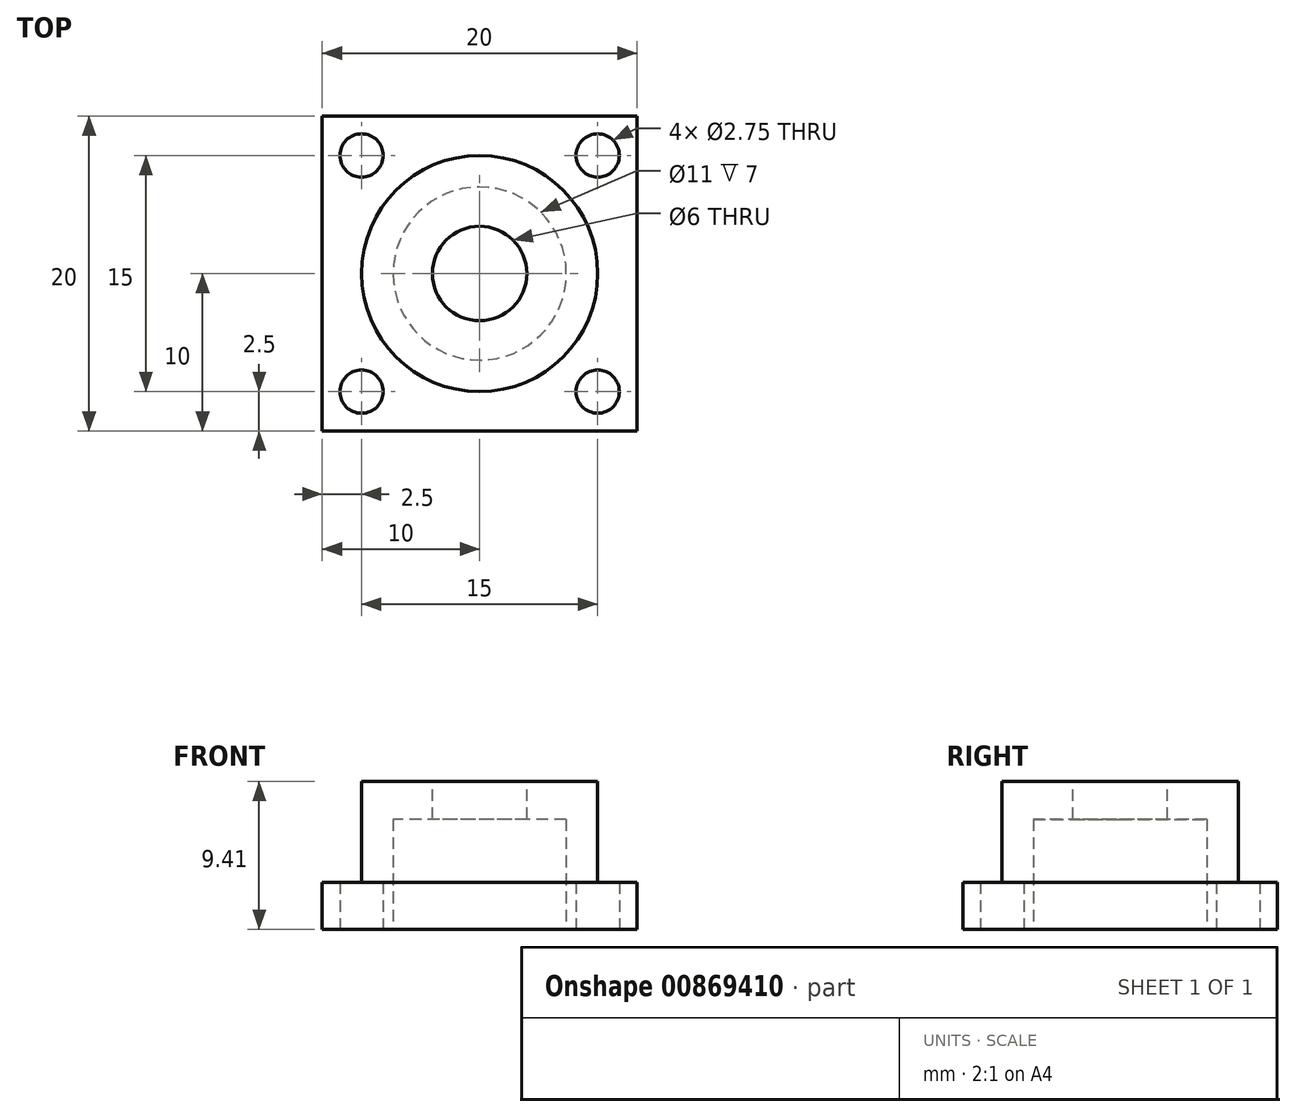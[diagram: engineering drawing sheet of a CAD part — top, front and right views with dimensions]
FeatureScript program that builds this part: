
annotation { "Feature Type Name" : "Feature", "Feature Type Description" : "" }
export const myFeature = defineFeature(function(context is Context, id is Id, definition is map)
    precondition{}
    {
        {
            var Q0;
            Q0=qCreatedBy(makeId("Top.planeOp"),FACE);
            var sketch = newSketch(context, id + "F0", { "sketchPlane" : qUnion([Q0])});
            skLineSegment(sketch, "E0.bottom", {"start": v(0, 0) * mm, "end": v(20, 0) * mm});
            skLineSegment(sketch, "E0.top", {"start": v(0, 20) * mm, "end": v(20, 20) * mm});
            skLineSegment(sketch, "E0.left", {"start": v(0, 0) * mm, "end": v(0, 20) * mm});
            skLineSegment(sketch, "E0.right", {"start": v(20, 0) * mm, "end": v(20, 20) * mm});
            skLineSegment(sketch, "E1", {"start": v(0, 10) * mm, "end": v(20, 10) * mm, "construction": true});
            skLineSegment(sketch, "E2", {"start": v(10, 0) * mm, "end": v(10, 20) * mm, "construction": true});
            skCircle(sketch, "E3", {"center": v(10, 10) * mm, "radius": 5.5 * mm});
            skCircle(sketch, "E4", {"center": v(2.5, 2.5) * mm, "radius": 1.38 * mm});
            skCircle(sketch, "E5.MirrorC", {"center": v(2.5, 17.5) * mm, "radius": 1.38 * mm});
            skCircle(sketch, "E6.MirrorC", {"center": v(17.5, 17.5) * mm, "radius": 1.38 * mm});
            skCircle(sketch, "E7.MirrorC", {"center": v(17.5, 2.5) * mm, "radius": 1.38 * mm});
            skSolve(sketch);
        }
        {
            var Q0;
            Q0=makeQuery(id+"F0.imprint","IMPRINT",FACE,{"disambiguationData":[TD([[makeQuery(id+"F0.imprint","IMPRINT",EDGE,{"derivedFrom":sQuery(id+"F0.wireOp",EDGE,"E0.bottom")}),1.0]])]});
            extrude(context, id + "F1", {"entities" : qUnion([Q0]), "depth" : 3 * mm, "offsetDistance" : 25 * mm});
        }
        {
            var Q0;
            Q0=makeQuery(id+"F1.opExtrude","CAP_FACE",FACE,{"disambiguationData":[OSD([sQuery(id+"F0.wireOp",EDGE,"E0.bottom"),sQuery(id+"F0.wireOp",EDGE,"E0.top"),sQuery(id+"F0.wireOp",EDGE,"E0.left"),sQuery(id+"F0.wireOp",EDGE,"E0.right"),sQuery(id+"F0.wireOp",EDGE,"E3"),sQuery(id+"F0.wireOp",EDGE,"E4"),sQuery(id+"F0.wireOp",EDGE,"E5.MirrorC"),sQuery(id+"F0.wireOp",EDGE,"E6.MirrorC"),sQuery(id+"F0.wireOp",EDGE,"E7.MirrorC")])],"isStart":false});
            var sketch = newSketch(context, id + "F2", { "sketchPlane" : qUnion([Q0])});
            skCircle(sketch, "E8", {"center": v(10, 10) * mm, "radius": 7.5 * mm});
            skCircle(sketch, "E9.0", {"center": v(10, 10) * mm, "radius": 5.5 * mm});
            skSolve(sketch);
        }
        {
            var Q0;
            Q0=makeQuery(id+"F2.imprint","IMPRINT",FACE,{"disambiguationData":[TD([[makeQuery(id+"F2.imprint","IMPRINT",EDGE,{"derivedFrom":sQuery(id+"F2.wireOp",EDGE,"E8")}),1.0]])]});
            extrude(context, id + "F3", {"entities" : qUnion([Q0]), "operationType" : NewBodyOperationType.ADD, "depth" : 4 * mm, "offsetDistance" : 25 * mm});
        }
        {
            var Q0;
            Q0=qCreatedBy(makeId("Front.planeOp"),FACE);
            cPlane(context, id + "F4", {"entities" : qUnion([Q0]), "cplaneType" : CPlaneType.OFFSET, "offset" : 10 * mm, "oppositeDirection" : true, "width" : 150 * mm, "height" : 150 * mm});
        }
        {
            var Q0;
            Q0=qCreatedBy(id+"F4.planeOp",FACE);
            var sketch = newSketch(context, id + "F5", { "sketchPlane" : qUnion([Q0])});
            skLineSegment(sketch, "E10.0", {"start": v(2.5, 7) * mm, "end": v(17.5, 7) * mm});
            skLineSegment(sketch, "E11", {"start": v(10, 7) * mm, "end": v(10, 0) * mm, "construction": true});
            skLineSegment(sketch, "E12", {"start": v(17.5, 7) * mm, "end": v(17.5, 9.41) * mm});
            skLineSegment(sketch, "E13", {"start": v(17.5, 9.41) * mm, "end": v(13, 9.41) * mm});
            skLineSegment(sketch, "E14", {"start": v(13, 9.41) * mm, "end": v(13, 7) * mm});
            skSolve(sketch);
        }
        {
            var Q0;
            {var subQ0=sQuery(id+"F5.wireOp",EDGE,"E12");Q0=makeQuery(id+"F5.imprint","IMPRINT",FACE,{"disambiguationData":[TD([[makeQuery(id+"F5.imprint","IMPRINT",EDGE,{"derivedFrom":subQ0}),1.0]])]});}
            var Q1;
            Q1=sQuery(id+"F5.wireOp",EDGE,"E11");
            revolve(context, id + "F6", {"operationType" : NewBodyOperationType.ADD, "surfaceOperationType" : NewSurfaceOperationType.NEW, "entities" : qUnion([Q0]), "axis" : qUnion([Q1]), "revolveType" : RevolveType.FULL});
        }
    });
